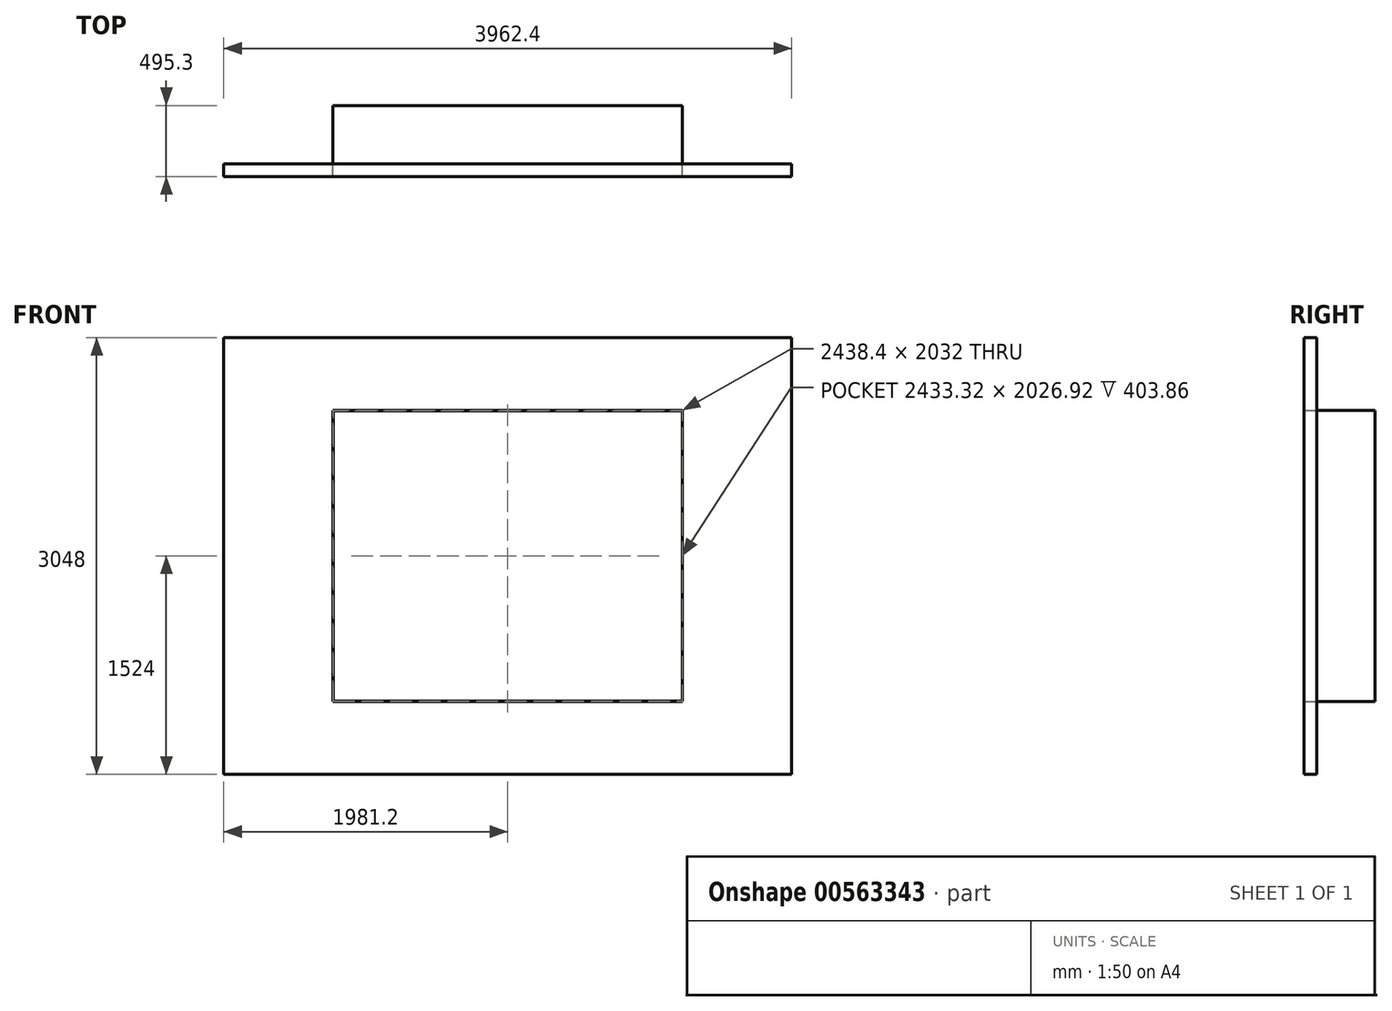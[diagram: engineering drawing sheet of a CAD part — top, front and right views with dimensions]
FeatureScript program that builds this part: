
annotation { "Feature Type Name" : "Feature", "Feature Type Description" : "" }
export const myFeature = defineFeature(function(context is Context, id is Id, definition is map)
    precondition{}
    {
        {
            var Q0;
            Q0=qCreatedBy(makeId("Front.planeOp"),FACE);
            var sketch = newSketch(context, id + "F0", { "sketchPlane" : qUnion([Q0])});
            skLineSegment(sketch, "E0.bottom", {"start": v(-1981.2, -1524) * mm, "end": v(1981.2, -1524) * mm});
            skLineSegment(sketch, "E0.top", {"start": v(-1981.2, 1524) * mm, "end": v(1981.2, 1524) * mm});
            skLineSegment(sketch, "E0.left", {"start": v(-1981.2, -1524) * mm, "end": v(-1981.2, 1524) * mm});
            skLineSegment(sketch, "E0.right", {"start": v(1981.2, -1524) * mm, "end": v(1981.2, 1524) * mm});
            skPoint(sketch, "E0.middle", {"position": v(0, 0) * mm});
            skLineSegment(sketch, "E1.bottom", {"start": v(-1219.2, -1016) * mm, "end": v(1219.2, -1016) * mm});
            skLineSegment(sketch, "E1.top", {"start": v(-1219.2, 1016) * mm, "end": v(1219.2, 1016) * mm});
            skLineSegment(sketch, "E1.left", {"start": v(-1219.2, -1016) * mm, "end": v(-1219.2, 1016) * mm});
            skLineSegment(sketch, "E1.right", {"start": v(1219.2, -1016) * mm, "end": v(1219.2, 1016) * mm});
            skSolve(sketch);
        }
        {
            var Q0;
            Q0 = qSketchRegion(id + "F0", true);
            extrude(context, id + "F1", {"entities" : qUnion([Q0]), "depth" : 88.9 * mm, "offsetDistance" : 25.4 * mm});
        }
        {
            var Q0;
            Q0=makeQuery(id+"F0.imprint","IMPRINT",FACE,{"disambiguationData":[TD([[makeQuery(id+"F0.imprint","IMPRINT",EDGE,{"derivedFrom":sQuery(id+"F0.wireOp",EDGE,"E1.bottom")}),1.0]])]});
            extrude(context, id + "F2", {"entities" : qUnion([Q0]), "oppositeDirection" : true, "depth" : 406.4 * mm, "offsetDistance" : 25.4 * mm});
        }
        {
            var Q0;
            Q0=makeQuery(id+"F2.opExtrude","CAP_FACE",FACE,{"disambiguationData":[OSD([sQuery(id+"F0.wireOp",EDGE,"E1.bottom"),sQuery(id+"F0.wireOp",EDGE,"E1.top"),sQuery(id+"F0.wireOp",EDGE,"E1.left"),sQuery(id+"F0.wireOp",EDGE,"E1.right")])],"isStart":true});
            shell(context, id + "F3", {"entities" : qUnion([Q0]), "thickness" : 2.54 * mm});
        }
    });
